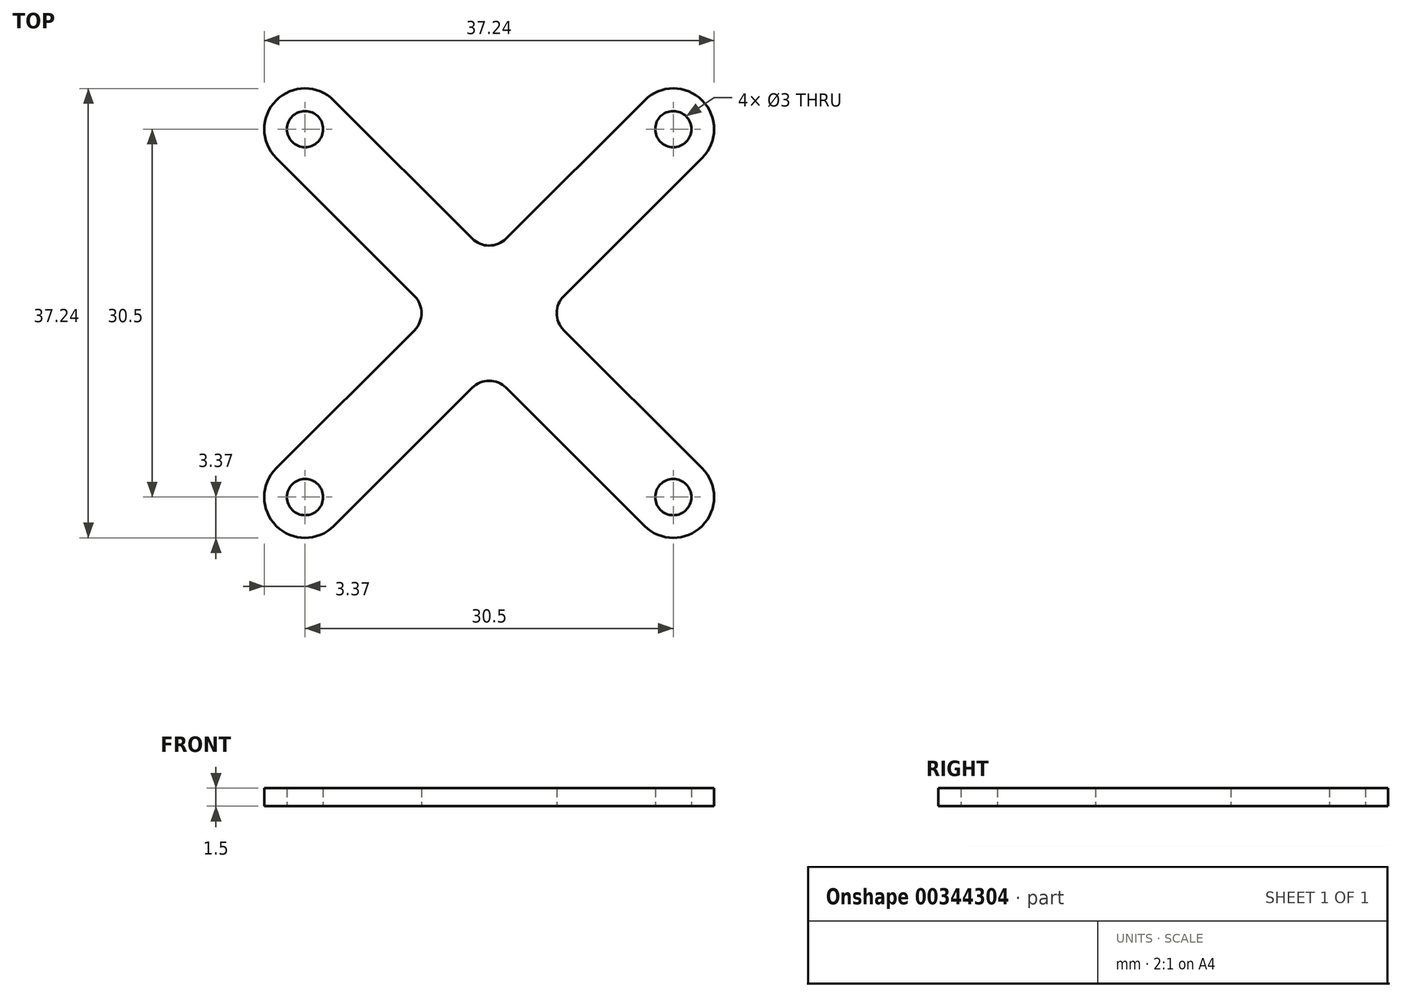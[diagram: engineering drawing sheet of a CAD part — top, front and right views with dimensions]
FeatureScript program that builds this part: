
annotation { "Feature Type Name" : "Feature", "Feature Type Description" : "" }
export const myFeature = defineFeature(function(context is Context, id is Id, definition is map)
    precondition{}
    {
        {
            var Q0;
            Q0=qCreatedBy(makeId("Top.planeOp"),FACE);
            var sketch = newSketch(context, id + "F0", { "sketchPlane" : qUnion([Q0])});
            skLineSegment(sketch, "E0.bottom", {"start": v(15.25, 15.25) * mm, "end": v(-15.25, 15.25) * mm, "construction": true});
            skLineSegment(sketch, "E0.top", {"start": v(15.25, -15.25) * mm, "end": v(-15.25, -15.25) * mm, "construction": true});
            skLineSegment(sketch, "E0.left", {"start": v(15.25, 15.25) * mm, "end": v(15.25, -15.25) * mm, "construction": true});
            skLineSegment(sketch, "E0.right", {"start": v(-15.25, 15.25) * mm, "end": v(-15.25, -15.25) * mm, "construction": true});
            skPoint(sketch, "E0.middle", {"position": v(0, 0) * mm});
            skLineSegment(sketch, "E1", {"start": v(-15.25, 15.25) * mm, "end": v(15.25, -15.25) * mm, "construction": true});
            skLineSegment(sketch, "E2", {"start": v(15.25, 15.25) * mm, "end": v(-15.25, -15.25) * mm, "construction": true});
            skLineSegment(sketch, "E3.0", {"start": v(-17.64, 12.86) * mm, "end": v(-6.19, 1.41) * mm});
            skLineSegment(sketch, "E4.0", {"start": v(-12.86, 17.64) * mm, "end": v(-1.41, 6.19) * mm});
            skLineSegment(sketch, "E5.0", {"start": v(12.86, 17.64) * mm, "end": v(1.41, 6.19) * mm});
            skLineSegment(sketch, "E6.0", {"start": v(17.64, 12.86) * mm, "end": v(6.19, 1.41) * mm});
            skCircle(sketch, "E7", {"center": v(-15.25, -15.25) * mm, "radius": 1.5 * mm});
            skCircle(sketch, "E8", {"center": v(-15.25, 15.25) * mm, "radius": 1.5 * mm});
            skCircle(sketch, "E9", {"center": v(15.25, 15.25) * mm, "radius": 1.5 * mm});
            skCircle(sketch, "E10", {"center": v(15.25, -15.25) * mm, "radius": 1.5 * mm});
            skArc(sketch, "E11", {"start": v(-17.64, 12.86) * mm, "mid": v(-17.64, 17.64) * mm, "end": v(-12.86, 17.64) * mm});
            skArc(sketch, "E12", {"start": v(12.86, 17.64) * mm, "mid": v(17.64, 17.64) * mm, "end": v(17.64, 12.86) * mm});
            skArc(sketch, "E13", {"start": v(17.64, -12.86) * mm, "mid": v(17.64, -17.64) * mm, "end": v(12.86, -17.64) * mm});
            skArc(sketch, "E14", {"start": v(-12.86, -17.64) * mm, "mid": v(-17.64, -17.64) * mm, "end": v(-17.64, -12.86) * mm});
            skLineSegment(sketch, "E15.trimOffspring", {"start": v(1.41, -6.19) * mm, "end": v(12.86, -17.64) * mm});
            skLineSegment(sketch, "E16.trimOffspring", {"start": v(-1.41, -6.19) * mm, "end": v(-12.86, -17.64) * mm});
            skLineSegment(sketch, "E17.trimOffspring", {"start": v(6.19, -1.41) * mm, "end": v(17.64, -12.86) * mm});
            skLineSegment(sketch, "E18.trimOffspring", {"start": v(-6.19, -1.41) * mm, "end": v(-17.64, -12.86) * mm});
            skPoint(sketch, "E19.visualSharp", {"position": v(-4.77, 0) * mm});
            skArc(sketch, "E19.filletArc", {"start": v(-6.19, -1.41) * mm, "mid": v(-5.6, 0) * mm, "end": v(-6.19, 1.41) * mm});
            skPoint(sketch, "E20.visualSharp", {"position": v(0, -4.77) * mm});
            skArc(sketch, "E20.filletArc", {"start": v(1.41, -6.19) * mm, "mid": v(0, -5.6) * mm, "end": v(-1.41, -6.19) * mm});
            skPoint(sketch, "E21.visualSharp", {"position": v(4.77, 0) * mm});
            skArc(sketch, "E21.filletArc", {"start": v(6.19, 1.41) * mm, "mid": v(5.6, 0) * mm, "end": v(6.19, -1.41) * mm});
            skPoint(sketch, "E22.visualSharp", {"position": v(0, 4.77) * mm});
            skArc(sketch, "E22.filletArc", {"start": v(-1.41, 6.19) * mm, "mid": v(0, 5.6) * mm, "end": v(1.41, 6.19) * mm});
            skSolve(sketch);
        }
        {
            var Q0;
            Q0=makeQuery(id+"F0.imprint","IMPRINT",FACE,{"disambiguationData":[TD([[makeQuery(id+"F0.imprint","IMPRINT",EDGE,{"derivedFrom":sQuery(id+"F0.wireOp",EDGE,"E3.0")}),1.0]])]});
            extrude(context, id + "F1", {"entities" : qUnion([Q0]), "depth" : 1.5 * mm});
        }
    });
